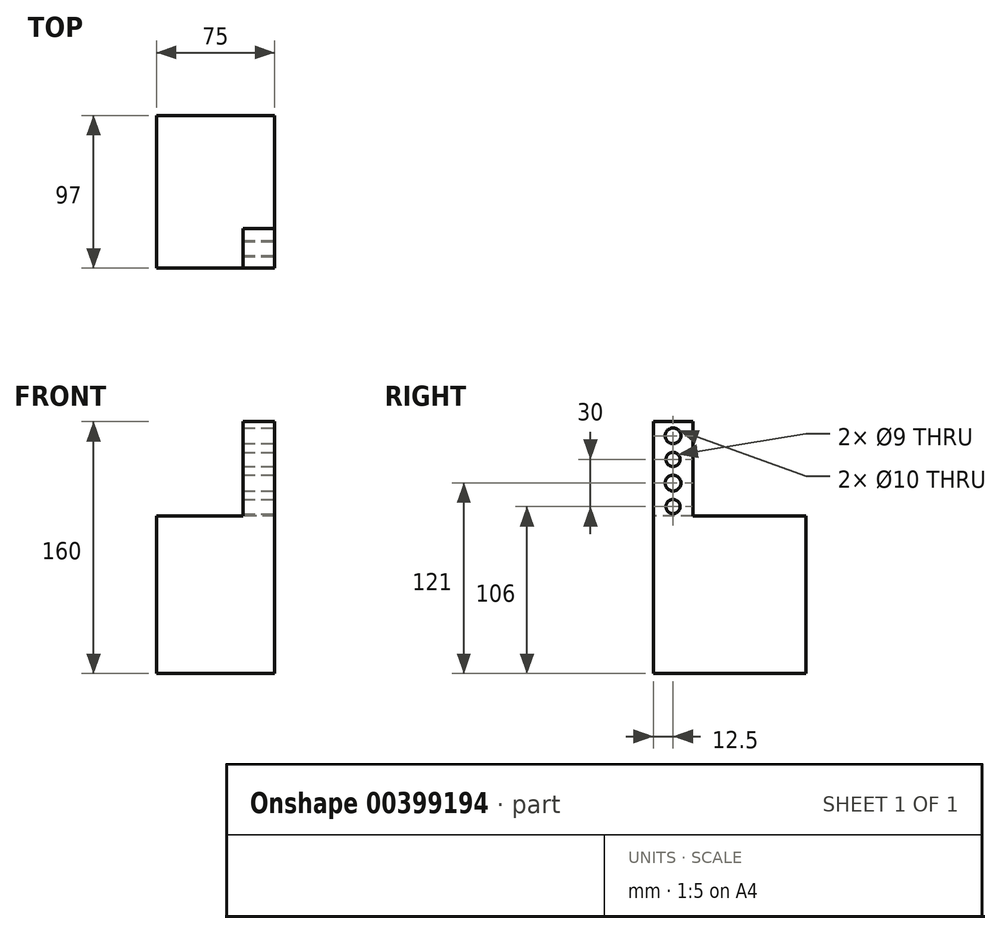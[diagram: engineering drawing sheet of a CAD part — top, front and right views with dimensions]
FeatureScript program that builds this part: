
annotation { "Feature Type Name" : "Feature", "Feature Type Description" : "" }
export const myFeature = defineFeature(function(context is Context, id is Id, definition is map)
    precondition{}
    {
        {
            var Q0;
            Q0=qCreatedBy(makeId("Top.planeOp"),FACE);
            var sketch = newSketch(context, id + "F0", { "sketchPlane" : qUnion([Q0])});
            skLineSegment(sketch, "E0.bottom", {"start": v(0, 0) * mm, "end": v(20, 0) * mm});
            skLineSegment(sketch, "E0.top", {"start": v(0, -25) * mm, "end": v(20, -25) * mm});
            skLineSegment(sketch, "E0.left", {"start": v(0, 0) * mm, "end": v(0, -25) * mm});
            skLineSegment(sketch, "E0.right", {"start": v(20, 0) * mm, "end": v(20, -25) * mm});
            skSolve(sketch);
        }
        {
            var Q0;
            Q0=qSketchRegion(id+"F0",true);
            extrude(context, id + "F1", {"entities" : qUnion([Q0]), "depth" : 80 * mm});
        }
        {
            var Q0;
            Q0=makeQuery(id+"F1.opExtrude","SWEPT_FACE",FACE,{"disambiguationData":[OSD([sQuery(id+"F0.wireOp",EDGE,"E0.right")])]});
            var sketch = newSketch(context, id + "F2", { "sketchPlane" : qUnion([Q0])});
            skLineSegment(sketch, "E1", {"start": v(-12.5, 80) * mm, "end": v(-12.5, 71) * mm, "construction": true});
            skPoint(sketch, "E1.endSnap0", {"position": v(-12.5, 80) * mm});
            skLineSegment(sketch, "E2", {"start": v(-12.5, 71) * mm, "end": v(-12.5, 56) * mm, "construction": true});
            skLineSegment(sketch, "E3", {"start": v(-12.5, 56) * mm, "end": v(-12.5, 41) * mm, "construction": true});
            skLineSegment(sketch, "E4", {"start": v(-12.5, 41) * mm, "end": v(-12.5, 26) * mm, "construction": true});
            skLineSegment(sketch, "E5", {"start": v(-12.5, 26) * mm, "end": v(-12.5, 0) * mm, "construction": true});
            skCircle(sketch, "E6", {"center": v(-12.5, 71) * mm, "radius": 5 * mm});
            skCircle(sketch, "E7", {"center": v(-12.5, 56) * mm, "radius": 4.5 * mm});
            skCircle(sketch, "E8", {"center": v(-12.5, 41) * mm, "radius": 5 * mm});
            skCircle(sketch, "E9", {"center": v(-12.5, 26) * mm, "radius": 4.5 * mm});
            skSolve(sketch);
        }
        {
            var Q0;
            Q0=qSketchRegion(id+"F2",true);
            extrude(context, id + "F3", {"entities" : qUnion([Q0]), "operationType" : NewBodyOperationType.REMOVE, "oppositeDirection" : true, "depth" : 25 * mm});
        }
        {
            var Q0;
            Q0=makeQuery(id+"F1.opExtrude","SWEPT_FACE",FACE,{"disambiguationData":[OSD([sQuery(id+"F0.wireOp",EDGE,"E0.bottom")])]});
            var sketch = newSketch(context, id + "F4", { "sketchPlane" : qUnion([Q0])});
            skLineSegment(sketch, "E10.bottom", {"start": v(-20, 0) * mm, "end": v(0, 0) * mm});
            skLineSegment(sketch, "E10.top", {"start": v(-20, 20) * mm, "end": v(0, 20) * mm});
            skLineSegment(sketch, "E10.left", {"start": v(-20, 0) * mm, "end": v(-20, 20) * mm});
            skLineSegment(sketch, "E10.right", {"start": v(0, 0) * mm, "end": v(0, 20) * mm});
            skSolve(sketch);
        }
        {
            var Q0;
            Q0 = qSketchRegion(id + "F4", true);
            extrude(context, id + "F5", {"entities" : qUnion([Q0]), "operationType" : NewBodyOperationType.ADD, "depth" : 72 * mm});
        }
        {
            var Q0;
            Q0=makeQuery(id+"F5.boolean.opBoolean","MERGE",FACE,{"derivedFrom":[makeQuery(id+"F1.opExtrude","SWEPT_FACE",FACE,{"disambiguationData":[OSD([sQuery(id+"F0.wireOp",EDGE,"E0.left")])]}),makeQuery(id+"F5.opExtrude","SWEPT_FACE",FACE,{"disambiguationData":[OSD([sQuery(id+"F4.wireOp",EDGE,"E10.right")])]})]});
            var sketch = newSketch(context, id + "F6", { "sketchPlane" : qUnion([Q0])});
            skLineSegment(sketch, "E11.bottom", {"start": v(-72, 20) * mm, "end": v(25, 20) * mm});
            skLineSegment(sketch, "E11.top", {"start": v(-72, 0) * mm, "end": v(25, 0) * mm});
            skLineSegment(sketch, "E11.left", {"start": v(-72, 20) * mm, "end": v(-72, 0) * mm});
            skLineSegment(sketch, "E11.right", {"start": v(25, 20) * mm, "end": v(25, 0) * mm});
            skSolve(sketch);
        }
        {
            var Q0;
            Q0 = qSketchRegion(id + "F6", true);
            extrude(context, id + "F7", {"entities" : qUnion([Q0]), "operationType" : NewBodyOperationType.ADD, "depth" : 55 * mm});
        }
        {
            var Q0;
            Q0=makeQuery(id+"F7.boolean.opBoolean","MERGE",FACE,{"derivedFrom":[makeQuery(id+"F5.boolean.opBoolean","MERGE",FACE,{"derivedFrom":[makeQuery(id+"F1.opExtrude","CAP_FACE",FACE,{"disambiguationData":[OSD([sQuery(id+"F0.wireOp",EDGE,"E0.bottom"),sQuery(id+"F0.wireOp",EDGE,"E0.top"),sQuery(id+"F0.wireOp",EDGE,"E0.left"),sQuery(id+"F0.wireOp",EDGE,"E0.right")])],"isStart":true}),makeQuery(id+"F5.opExtrude","SWEPT_FACE",FACE,{"disambiguationData":[OSD([sQuery(id+"F4.wireOp",EDGE,"E10.bottom")])]})]}),makeQuery(id+"F7.opExtrude","SWEPT_FACE",FACE,{"disambiguationData":[OSD([sQuery(id+"F6.wireOp",EDGE,"E11.top")])]})]});
            var sketch = newSketch(context, id + "F8", { "sketchPlane" : qUnion([Q0])});
            skLineSegment(sketch, "E12.bottom", {"start": v(-55, 25) * mm, "end": v(20, 25) * mm});
            skLineSegment(sketch, "E12.top", {"start": v(-55, -72) * mm, "end": v(20, -72) * mm});
            skLineSegment(sketch, "E12.left", {"start": v(-55, 25) * mm, "end": v(-55, -72) * mm});
            skLineSegment(sketch, "E12.right", {"start": v(20, 25) * mm, "end": v(20, -72) * mm});
            skSolve(sketch);
        }
        {
            var Q0;
            Q0 = qSketchRegion(id + "F8", true);
            extrude(context, id + "F9", {"entities" : qUnion([Q0]), "operationType" : NewBodyOperationType.ADD, "depth" : 80 * mm});
        }
    });
